# Revit family: Genie_Site_ArticulatingBoom_(S-60J)
name_source: partatom
category: Site
revit_build: Autodesk Revit 2018 (Build: 20190510_1515(x64)
units: mm (PartAtom-declared; Revit-internal decimal feet)

## family parameters
Always vertical = Yes
Cut with Voids When Loaded = No
OmniClass Number = 23.50.85.17
OmniClass Title = Telescoping Platforms
Part Type = Normal
Round Connector Dimension = Use Diameter
Shared = No
Work Plane-Based = No

## types (1)
- S-60J
    Assembly Code = E1030900
    AssetType = Moveable
    BIMObjectName = Genie_Site_ArticulatingBoom_(S-60J)
    ClassificationName = Uniclass2015
    ClassificationValue = Pr_65_80_47_95
    Color = Grey & Blue
    Cost = 0 $
    Description = Right-sized for completing work-at-height applications, such as general construction, maintenance, inspection and painting tasks, the new Genie® S®-60 J telescopic boom lift offers the essential performance that operators need to get work done at height. It offers the right solution to get work done at height, including leading unrestricted platform capacity of 660 lb (300 kg), allowing for two occupants plus tools. With a standard 6 ft (1.8 m) jib, which leads the class in length and capacity for the 60-ft (18.3 m) height class. The Genie S-60 J is compact, low-weight design (16,650 lb / 7,550 kg) keeps ground pressure low when operators are working in more sensitive ground conditions. Additionally, rental companies can fit two units on one equipment truck, reducing shipping costs and increasing rROIC, thanks to the machine’s low weight and compact size.
    DocumentationLiterature = https://www.genielift.com
    DocumentationTechnical = https://www.genielift.com
    DurationUnit = Years
    ExpectedLife = 0
    Features = Suited for use in general construction, maintenance, inspection and painting tasks. Leading unrestricted platform capacity of 660 lb (300 kg) with 6-ft (1.8 m) jib. Low 16,650 lb (7550 kg) operating weight in a compact chassis design. Platform height of 60 ft 10 in (18.5 m) and horizontal reach of 40 ft 6 in (12.3 m). 1 ft 10 in (56.4 cm) of ground clearance to clear obstacles.
    Finish = Painted Steel
    IfcExportAs = IfcTransportElement
    IfcExportType = IfcTransportElementType
    Keynote = X
    Manufacturer = Genie
    ManufacturerName = Genie
    Material = Painted Steel
    Model = Genie - Articulating Boom
    ModelNumber = S-60J
    ModelReference = Genie - Articulating Boom
    NBSDescription = Vertical lifting platforms
    NBSObjectName = Genie - Vertical lifting platforms
    NBSReference = 90-80-65/350
    NominalDepth = 2490 mm
    NominalHeight = 2690 mm
    NominalLength = 9700 mm
    ProductionYear = 2020
    Size = 2.49m x 2.69m x 9.7m
    Type Comments = S-60J
    TypeName = Genie - Articulating Boom
    URL = http://www.genielift.co.uk
    WarrantyDurationLabor = 0
    WarrantyDurationParts = 0
    WarrantyDurationUnit = Years
    WarrantyGuarantorLabor = http://www.genielift.co.uk
    WarrantyGuarantorParts = http://www.genielift.co.uk
    _BSBibleVersion = 16
    _BimSpecGuid = 0
    _CurrentRevision = 1
    _DistributedBy = www.bimstore.co

## geometry (parser evidence)
native form markers: Sweep x28
no freeform markers — native parametric forms only
